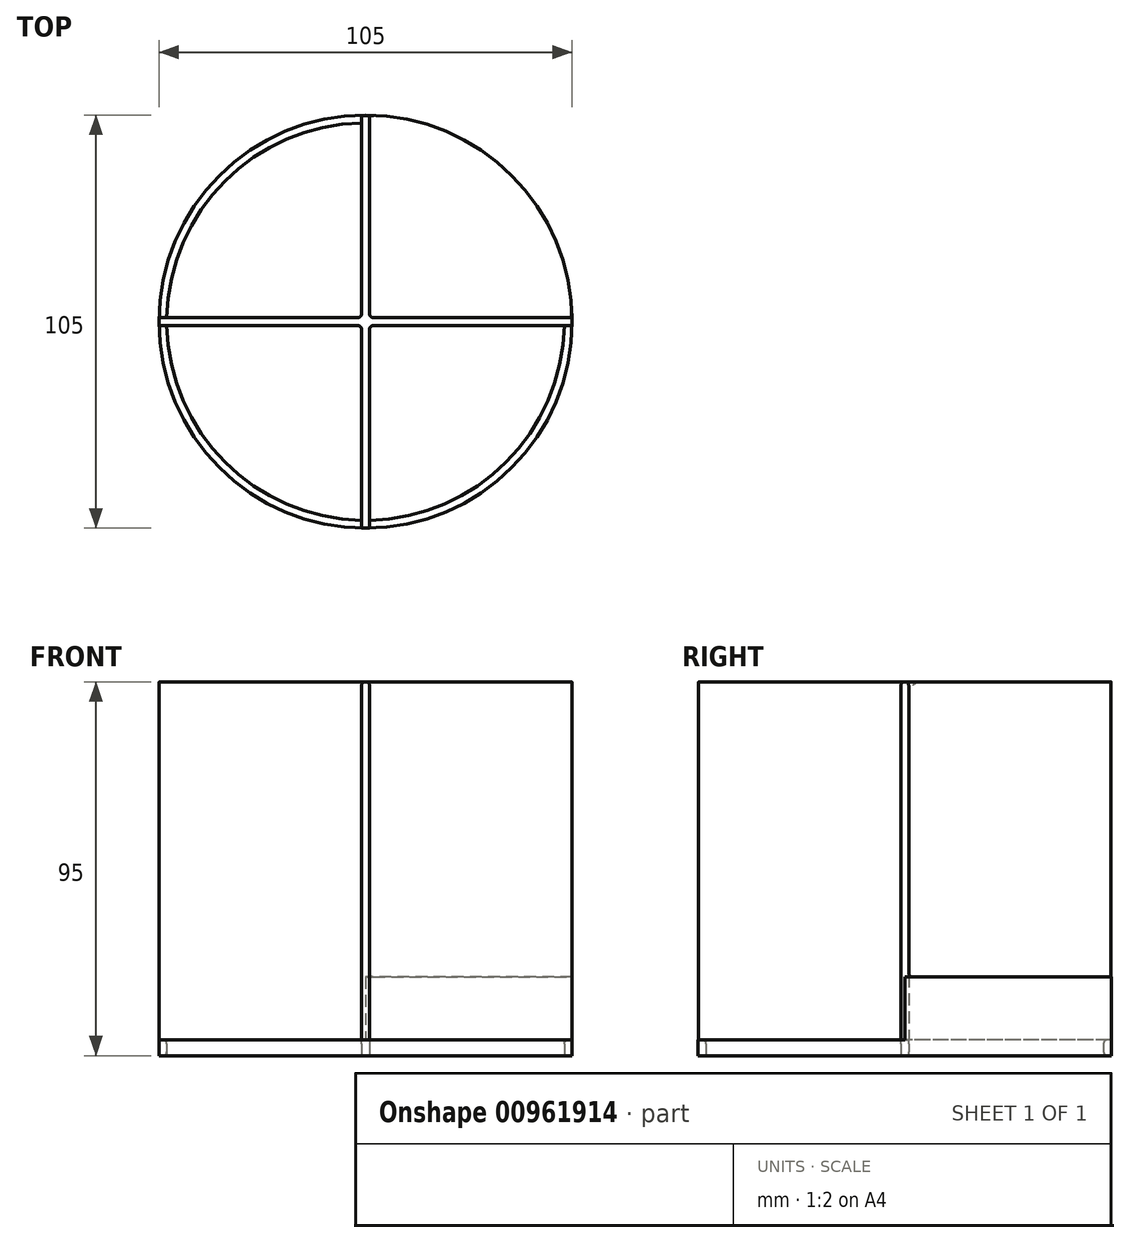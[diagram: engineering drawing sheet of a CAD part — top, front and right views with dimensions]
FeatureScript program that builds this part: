
annotation { "Feature Type Name" : "Feature", "Feature Type Description" : "" }
export const myFeature = defineFeature(function(context is Context, id is Id, definition is map)
    precondition{}
    {
        {
            var Q0;
            Q0=qCreatedBy(makeId("Top.planeOp"),FACE);
            var sketch = newSketch(context, id + "F0", { "sketchPlane" : qUnion([Q0])});
            skCircle(sketch, "E0", {"center": v(0, 0) * mm, "radius": 52.5 * mm});
            skCircle(sketch, "E1", {"center": v(0, 0) * mm, "radius": 50.5 * mm});
            skSolve(sketch);
        }
        {
            var Q0;
            Q0 = qSketchRegion(id + "F0", true);
            extrude(context, id + "F1", {"entities" : qUnion([Q0]), "depth" : 4 * mm, "offsetDistance" : 25 * mm});
        }
        {
            var Q0;
            Q0=qCreatedBy(makeId("Top.planeOp"),FACE);
            var sketch = newSketch(context, id + "F2", { "sketchPlane" : qUnion([Q0])});
            skLineSegment(sketch, "E2.bottom", {"start": v(-1, -52.4) * mm, "end": v(1, -52.4) * mm});
            skLineSegment(sketch, "E2.top", {"start": v(-1, 52.4) * mm, "end": v(1, 52.4) * mm});
            skLineSegment(sketch, "E2.left", {"start": v(-1, -52.4) * mm, "end": v(-1, 52.4) * mm});
            skLineSegment(sketch, "E2.right", {"start": v(1, -52.4) * mm, "end": v(1, 52.4) * mm});
            skPoint(sketch, "E2.middle", {"position": v(0, 0) * mm});
            skLineSegment(sketch, "E3.bottom", {"start": v(-52.4, 1) * mm, "end": v(52.4, 1) * mm});
            skLineSegment(sketch, "E3.top", {"start": v(-52.4, -1) * mm, "end": v(52.4, -1) * mm});
            skLineSegment(sketch, "E3.left", {"start": v(-52.4, 1) * mm, "end": v(-52.4, -1) * mm});
            skLineSegment(sketch, "E3.right", {"start": v(52.4, 1) * mm, "end": v(52.4, -1) * mm});
            skSolve(sketch);
        }
        {
            var Q0;
            Q0 = qSketchRegion(id + "F2", true);
            extrude(context, id + "F3", {"entities" : qUnion([Q0]), "operationType" : NewBodyOperationType.ADD, "depth" : 95 * mm, "offsetDistance" : 25 * mm});
        }
        {
            var Q0;
            Q0=qCreatedBy(makeId("Top.planeOp"),FACE);
            var sketch = newSketch(context, id + "F4", { "sketchPlane" : qUnion([Q0])});
            skArc(sketch, "E4", {"start": v(52.5, 0) * mm, "mid": v(37.12, 37.12) * mm, "end": v(0, 52.5) * mm});
            skLineSegment(sketch, "E5", {"start": v(0, 0) * mm, "end": v(0, 52.5) * mm});
            skLineSegment(sketch, "E6", {"start": v(0, 0) * mm, "end": v(52.5, 0) * mm});
            skSolve(sketch);
        }
        {
            var Q0;
            Q0 = qSketchRegion(id + "F4", true);
            extrude(context, id + "F5", {"entities" : qUnion([Q0]), "operationType" : NewBodyOperationType.ADD, "depth" : 20 * mm, "offsetDistance" : 25 * mm});
        }
        {
            var Q0;
            Q0=makeQuery(id+"F3.opExtrude","SWEPT_EDGE",EDGE,{"disambiguationData":[OSD([sQuery(id+"F2.wireOp",EDGE,"E2.right"),sQuery(id+"F2.wireOp",EDGE,"E3.bottom")])]});
            var Q1;
            {var subQ0=sQuery(id+"F2.wireOp",EDGE,"E3.bottom");Q1=makeQuery(id+"F5.boolean.opBoolean","INTERSECT",EDGE,{"derivedFrom":[makeQuery(id+"F3.opExtrude","SWEPT_FACE",FACE,{"disambiguationData":[OSD([subQ0]),TDD([makeQuery(id+"F2.imprint","IMPRINT",EDGE,{"disambiguationData":[TD([[makeQuery(id+"F2.imprint","INTERSECT",VERTEX,{"derivedFrom":[subQ0,sQuery(id+"F2.wireOp",EDGE,"E3.right")]}),1.0]])],"derivedFrom":subQ0})])]}),makeQuery(id+"F5.opExtrude","CAP_FACE",FACE,{"disambiguationData":[OSD([sQuery(id+"F4.wireOp",EDGE,"E4"),sQuery(id+"F4.wireOp",EDGE,"E5"),sQuery(id+"F4.wireOp",EDGE,"E6")])],"isStart":false})]});}
            var Q2;
            {var subQ0=sQuery(id+"F2.wireOp",EDGE,"E2.right");Q2=makeQuery(id+"F5.boolean.opBoolean","INTERSECT",EDGE,{"derivedFrom":[makeQuery(id+"F3.opExtrude","SWEPT_FACE",FACE,{"disambiguationData":[OSD([subQ0]),TDD([makeQuery(id+"F2.imprint","IMPRINT",EDGE,{"disambiguationData":[TD([[makeQuery(id+"F2.imprint","INTERSECT",VERTEX,{"derivedFrom":[sQuery(id+"F2.wireOp",EDGE,"E2.top"),subQ0]}),1.0]])],"derivedFrom":subQ0})])]}),makeQuery(id+"F5.opExtrude","CAP_FACE",FACE,{"disambiguationData":[OSD([sQuery(id+"F4.wireOp",EDGE,"E4"),sQuery(id+"F4.wireOp",EDGE,"E5"),sQuery(id+"F4.wireOp",EDGE,"E6")])],"isStart":false})]});}
            var Q3;
            {var subQ0=sQuery(id+"F2.wireOp",EDGE,"E2.right");Q3=makeQuery(id+"F3.opExtrude","CAP_EDGE",EDGE,{"disambiguationData":[OSD([subQ0]),TDD([makeQuery(id+"F2.imprint","IMPRINT",EDGE,{"disambiguationData":[TD([[makeQuery(id+"F2.imprint","INTERSECT",VERTEX,{"derivedFrom":[sQuery(id+"F2.wireOp",EDGE,"E2.top"),subQ0]}),1.0]])],"derivedFrom":subQ0})])],"isStart":false});}
            var Q4;
            {var subQ0=sQuery(id+"F2.wireOp",EDGE,"E3.bottom");Q4=makeQuery(id+"F3.opExtrude","CAP_EDGE",EDGE,{"disambiguationData":[OSD([subQ0]),TDD([makeQuery(id+"F2.imprint","IMPRINT",EDGE,{"disambiguationData":[TD([[makeQuery(id+"F2.imprint","INTERSECT",VERTEX,{"derivedFrom":[subQ0,sQuery(id+"F2.wireOp",EDGE,"E3.right")]}),1.0]])],"derivedFrom":subQ0})])],"isStart":false});}
            var Q5;
            {var subQ0=sQuery(id+"F2.wireOp",EDGE,"E3.bottom");Q5=makeQuery(id+"F3.opExtrude","CAP_EDGE",EDGE,{"disambiguationData":[OSD([subQ0]),TDD([makeQuery(id+"F2.imprint","IMPRINT",EDGE,{"disambiguationData":[TD([[makeQuery(id+"F2.imprint","INTERSECT",VERTEX,{"derivedFrom":[subQ0,sQuery(id+"F2.wireOp",EDGE,"E3.left")]}),-1.0]])],"derivedFrom":subQ0})])],"isStart":false});}
            var Q6;
            Q6=makeQuery(id+"F3.opExtrude","SWEPT_EDGE",EDGE,{"disambiguationData":[OSD([sQuery(id+"F2.wireOp",EDGE,"E2.left"),sQuery(id+"F2.wireOp",EDGE,"E3.bottom")])]});
            var Q7;
            Q7=makeQuery(id+"F3.opExtrude","SWEPT_EDGE",EDGE,{"disambiguationData":[OSD([sQuery(id+"F2.wireOp",EDGE,"E2.right"),sQuery(id+"F2.wireOp",EDGE,"E3.top")])]});
            var Q8;
            Q8=makeQuery(id+"F3.opExtrude","SWEPT_EDGE",EDGE,{"disambiguationData":[OSD([sQuery(id+"F2.wireOp",EDGE,"E2.left"),sQuery(id+"F2.wireOp",EDGE,"E3.top")])]});
            var Q9;
            {var subQ0=sQuery(id+"F0.wireOp",EDGE,"E1");var subQ1=sQuery(id+"F2.wireOp",EDGE,"E2.left");Q9=makeQuery(id+"F3.boolean.opBoolean","SPLIT",EDGE,{"disambiguationData":[TD([makeQuery(id+"F3.opExtrude","SWEPT_FACE",FACE,{"disambiguationData":[OSD([subQ1]),TDD([makeQuery(id+"F2.imprint","IMPRINT",EDGE,{"disambiguationData":[TD([[makeQuery(id+"F2.imprint","INTERSECT",VERTEX,{"derivedFrom":[sQuery(id+"F2.wireOp",EDGE,"E2.bottom"),subQ1]}),-1.0]])],"derivedFrom":subQ1})])]})])],"derivedFrom":makeQuery(id+"F1.opExtrude","CAP_EDGE",EDGE,{"disambiguationData":[OSD([subQ0])],"isStart":false})});}
            var Q10;
            {var subQ0=sQuery(id+"F0.wireOp",EDGE,"E1");var subQ1=sQuery(id+"F2.wireOp",EDGE,"E2.right");Q10=makeQuery(id+"F3.boolean.opBoolean","SPLIT",EDGE,{"disambiguationData":[TD([makeQuery(id+"F3.opExtrude","SWEPT_FACE",FACE,{"disambiguationData":[OSD([subQ1]),TDD([makeQuery(id+"F2.imprint","IMPRINT",EDGE,{"disambiguationData":[TD([[makeQuery(id+"F2.imprint","INTERSECT",VERTEX,{"derivedFrom":[sQuery(id+"F2.wireOp",EDGE,"E2.bottom"),subQ1]}),-1.0]])],"derivedFrom":subQ1})])]})])],"derivedFrom":makeQuery(id+"F1.opExtrude","CAP_EDGE",EDGE,{"disambiguationData":[OSD([subQ0])],"isStart":false})});}
            var Q11;
            {var subQ2=sQuery(id+"F2.wireOp",EDGE,"E2.left");var subQ3=sQuery(id+"F2.wireOp",EDGE,"E2.top");var subQ5=sQuery(id+"F0.wireOp",EDGE,"E1");Q11=makeQuery(id+"F3.boolean.opBoolean","SPLIT",EDGE,{"disambiguationData":[TD([makeQuery(id+"F3.opExtrude","SWEPT_FACE",FACE,{"disambiguationData":[OSD([subQ2]),TDD([makeQuery(id+"F2.imprint","IMPRINT",EDGE,{"disambiguationData":[TD([[makeQuery(id+"F2.imprint","INTERSECT",VERTEX,{"derivedFrom":[subQ3,subQ2]}),1.0]])],"derivedFrom":subQ2})])]})])],"derivedFrom":makeQuery(id+"F1.opExtrude","CAP_EDGE",EDGE,{"disambiguationData":[OSD([subQ5])],"isStart":true})});}
            var Q12;
            {var subQ0=sQuery(id+"F0.wireOp",EDGE,"E1");var subQ1=sQuery(id+"F2.wireOp",EDGE,"E2.left");Q12=makeQuery(id+"F3.boolean.opBoolean","SPLIT",EDGE,{"disambiguationData":[TD([makeQuery(id+"F3.opExtrude","SWEPT_FACE",FACE,{"disambiguationData":[OSD([subQ1]),TDD([makeQuery(id+"F2.imprint","IMPRINT",EDGE,{"disambiguationData":[TD([[makeQuery(id+"F2.imprint","INTERSECT",VERTEX,{"derivedFrom":[sQuery(id+"F2.wireOp",EDGE,"E2.top"),subQ1]}),1.0]])],"derivedFrom":subQ1})])]})])],"derivedFrom":makeQuery(id+"F1.opExtrude","CAP_EDGE",EDGE,{"disambiguationData":[OSD([subQ0])],"isStart":false})});}
            fillet(context, id + "F6", {"entities" : qUnion([Q0, Q1, Q2, Q3, Q4, Q5, Q6, Q7, Q8, Q9, Q10, Q11, Q12]), "radius" : 1 * mm, "tangentPropagation" : true, "allowEdgeOverflow" : false});
        }
        {
            var Q0;
            {var subQ0=sQuery(id+"F2.wireOp",EDGE,"E2.right");Q0=makeQuery(id+"F3.opExtrude","CAP_EDGE",EDGE,{"disambiguationData":[OSD([subQ0]),TDD([makeQuery(id+"F2.imprint","IMPRINT",EDGE,{"disambiguationData":[TD([[makeQuery(id+"F2.imprint","INTERSECT",VERTEX,{"derivedFrom":[sQuery(id+"F2.wireOp",EDGE,"E2.bottom"),subQ0]}),-1.0]])],"derivedFrom":subQ0})])],"isStart":false});}
            var Q1;
            {var subQ0=sQuery(id+"F2.wireOp",EDGE,"E2.left");Q1=makeQuery(id+"F3.opExtrude","CAP_EDGE",EDGE,{"disambiguationData":[OSD([subQ0]),TDD([makeQuery(id+"F2.imprint","IMPRINT",EDGE,{"disambiguationData":[TD([[makeQuery(id+"F2.imprint","INTERSECT",VERTEX,{"derivedFrom":[sQuery(id+"F2.wireOp",EDGE,"E2.bottom"),subQ0]}),-1.0]])],"derivedFrom":subQ0})])],"isStart":false});}
            var Q2;
            {var subQ0=sQuery(id+"F2.wireOp",EDGE,"E3.top");Q2=makeQuery(id+"F3.opExtrude","CAP_EDGE",EDGE,{"disambiguationData":[OSD([subQ0]),TDD([makeQuery(id+"F2.imprint","IMPRINT",EDGE,{"disambiguationData":[TD([[makeQuery(id+"F2.imprint","INTERSECT",VERTEX,{"derivedFrom":[subQ0,sQuery(id+"F2.wireOp",EDGE,"E3.left")]}),-1.0]])],"derivedFrom":subQ0})])],"isStart":false});}
            var Q3;
            {var subQ0=sQuery(id+"F2.wireOp",EDGE,"E3.top");Q3=makeQuery(id+"F3.opExtrude","CAP_EDGE",EDGE,{"disambiguationData":[OSD([subQ0]),TDD([makeQuery(id+"F2.imprint","IMPRINT",EDGE,{"disambiguationData":[TD([[makeQuery(id+"F2.imprint","INTERSECT",VERTEX,{"derivedFrom":[subQ0,sQuery(id+"F2.wireOp",EDGE,"E3.right")]}),1.0]])],"derivedFrom":subQ0})])],"isStart":false});}
            fillet(context, id + "F7", {"entities" : qUnion([Q0, Q1, Q2, Q3]), "radius" : 1 * mm, "tangentPropagation" : true, "allowEdgeOverflow" : false});
        }
    });
